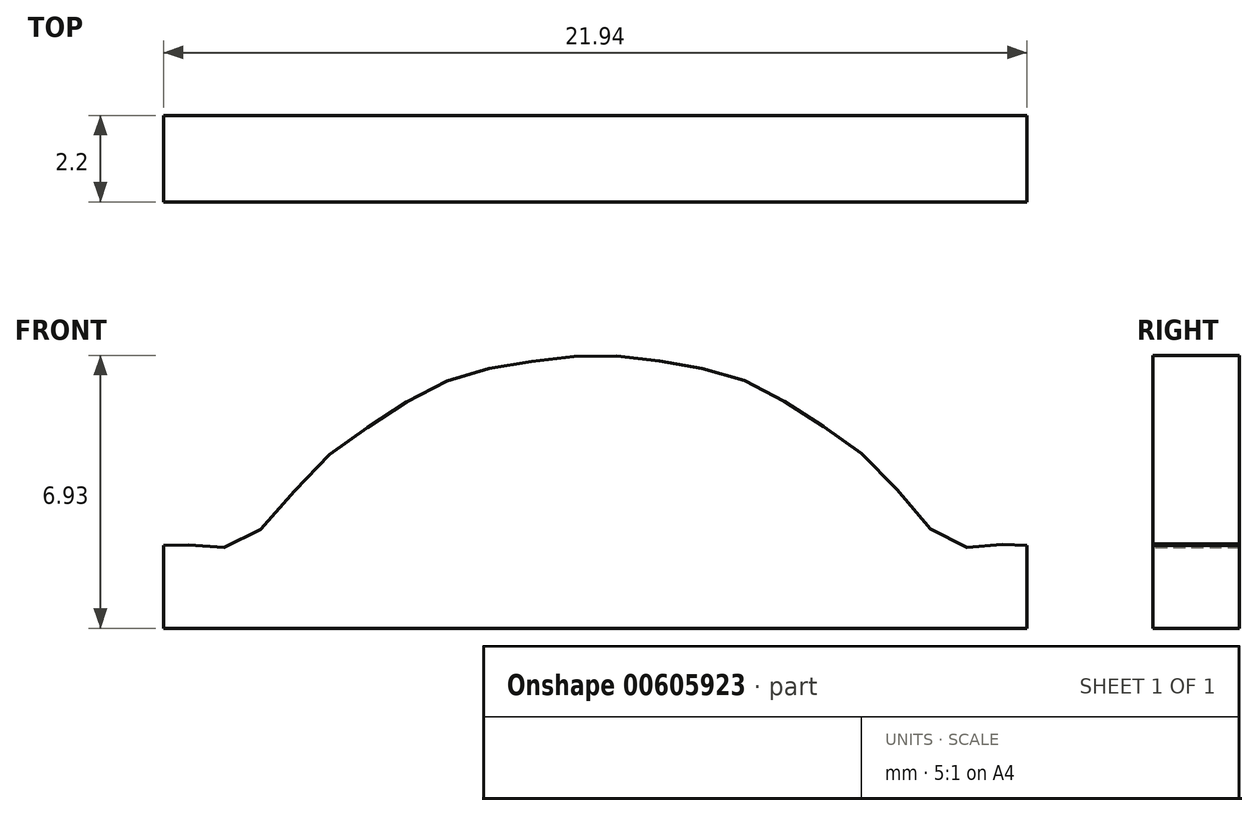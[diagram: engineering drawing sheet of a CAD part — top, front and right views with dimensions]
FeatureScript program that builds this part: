
annotation { "Feature Type Name" : "Feature", "Feature Type Description" : "" }
export const myFeature = defineFeature(function(context is Context, id is Id, definition is map)
    precondition{}
    {
        {
            var Q0;
            Q0=qCreatedBy(makeId("Front.planeOp"),FACE);
            var sketch = newSketch(context, id + "F0", { "sketchPlane" : qUnion([Q0])});
            skLineSegment(sketch, "E0", {"start": v(11, -3.43) * mm, "end": v(-11, -3.43) * mm});
            skLineSegment(sketch, "E1", {"start": v(-10.1, -3.43) * mm, "end": v(-9.17, -1.04) * mm});
            skLineSegment(sketch, "E2", {"start": v(-9.17, -1.04) * mm, "end": v(-8.25, -3.44) * mm});
            skLineSegment(sketch, "E3", {"start": v(-8.25, -3.44) * mm, "end": v(-7.33, 0.38) * mm});
            skLineSegment(sketch, "E4", {"start": v(-7.33, 0.38) * mm, "end": v(-6.42, -3.44) * mm});
            skLineSegment(sketch, "E5", {"start": v(-6.42, -3.44) * mm, "end": v(-5.5, 1.8) * mm});
            skLineSegment(sketch, "E6", {"start": v(-5.5, 1.81) * mm, "end": v(-4.58, -3.43) * mm});
            skLineSegment(sketch, "E7", {"start": v(-4.57, -3.43) * mm, "end": v(-3.67, 2.79) * mm});
            skLineSegment(sketch, "E8", {"start": v(-3.67, 2.8) * mm, "end": v(-2.75, -3.43) * mm});
            skLineSegment(sketch, "E9", {"start": v(-2.75, -3.43) * mm, "end": v(-1.83, 3.28) * mm});
            skLineSegment(sketch, "E10", {"start": v(-1.83, 3.28) * mm, "end": v(-0.92, -3.43) * mm});
            skLineSegment(sketch, "E11", {"start": v(9.16, -1.04) * mm, "end": v(8.24, -3.44) * mm});
            skLineSegment(sketch, "E12", {"start": v(8.24, -3.44) * mm, "end": v(7.32, 0.38) * mm});
            skLineSegment(sketch, "E13", {"start": v(7.32, 0.38) * mm, "end": v(6.4, -3.44) * mm});
            skLineSegment(sketch, "E14", {"start": v(6.4, -3.44) * mm, "end": v(5.49, 1.8) * mm});
            skLineSegment(sketch, "E15", {"start": v(5.49, 1.81) * mm, "end": v(4.57, -3.43) * mm});
            skLineSegment(sketch, "E16", {"start": v(4.56, -3.43) * mm, "end": v(3.66, 2.79) * mm});
            skLineSegment(sketch, "E17", {"start": v(3.66, 2.8) * mm, "end": v(2.74, -3.43) * mm});
            skLineSegment(sketch, "E18", {"start": v(2.74, -3.43) * mm, "end": v(1.82, 3.28) * mm});
            skLineSegment(sketch, "E19", {"start": v(1.82, 3.28) * mm, "end": v(0.9, -3.43) * mm});
            skLineSegment(sketch, "E20", {"start": v(0.9, -3.43) * mm, "end": v(-0.01, 3.44) * mm});
            skFitSpline(sketch, "E21", {"points": [v(-11, -1.33) * mm, v(-9.17, -1.04) * mm, v(-7.33, 0.38) * mm, v(-5.5, 1.81) * mm, v(-3.67, 2.8) * mm, v(-1.83, 3.28) * mm, v(-0.01, 3.44) * mm, v(1.82, 3.28) * mm, v(3.66, 2.8) * mm, v(5.49, 1.81) * mm, v(7.32, 0.38) * mm, v(9.16, -1.04) * mm, v(10.94, -1.33) * mm], "startDerivative": vector(23.69, 0.54) * mm, "endDerivative": vector(23.24, -1.18) * mm});
            skSolve(sketch);
        }
        {
            var Q0;
            Q0=qCreatedBy(makeId("Front.planeOp"),FACE);
            var sketch = newSketch(context, id + "F1", { "sketchPlane" : qUnion([Q0])});
            skLineSegment(sketch, "E22", {"start": v(-11, -1.33) * mm, "end": v(-11, -3.43) * mm});
            skLineSegment(sketch, "E23", {"start": v(-11, -3.43) * mm, "end": v(10.94, -3.43) * mm});
            skLineSegment(sketch, "E24", {"start": v(10.94, -3.43) * mm, "end": v(10.94, -1.33) * mm});
            skFitSpline(sketch, "E25.0", {"points": [v(-11, -1.33) * mm, v(-10.37, -1.31) * mm, v(-9.05, -1.28) * mm, v(-7.34, 0.44) * mm, v(-5.55, 1.85) * mm, v(-3.71, 2.88) * mm, v(-1.84, 3.32) * mm, v(-0.01, 3.5) * mm, v(1.83, 3.32) * mm, v(3.7, 2.88) * mm, v(5.54, 1.85) * mm, v(7.33, 0.44) * mm, v(9.03, -1.28) * mm, v(10.33, -1.3) * mm, v(10.94, -1.33) * mm]});
            skSolve(sketch);
        }
        {
            var Q0;
            Q0 = qSketchRegion(id + "F1", true);
            extrude(context, id + "F2", {"entities" : qUnion([Q0]), "depth" : 2.2 * mm, "offsetDistance" : 25 * mm});
        }
    });
